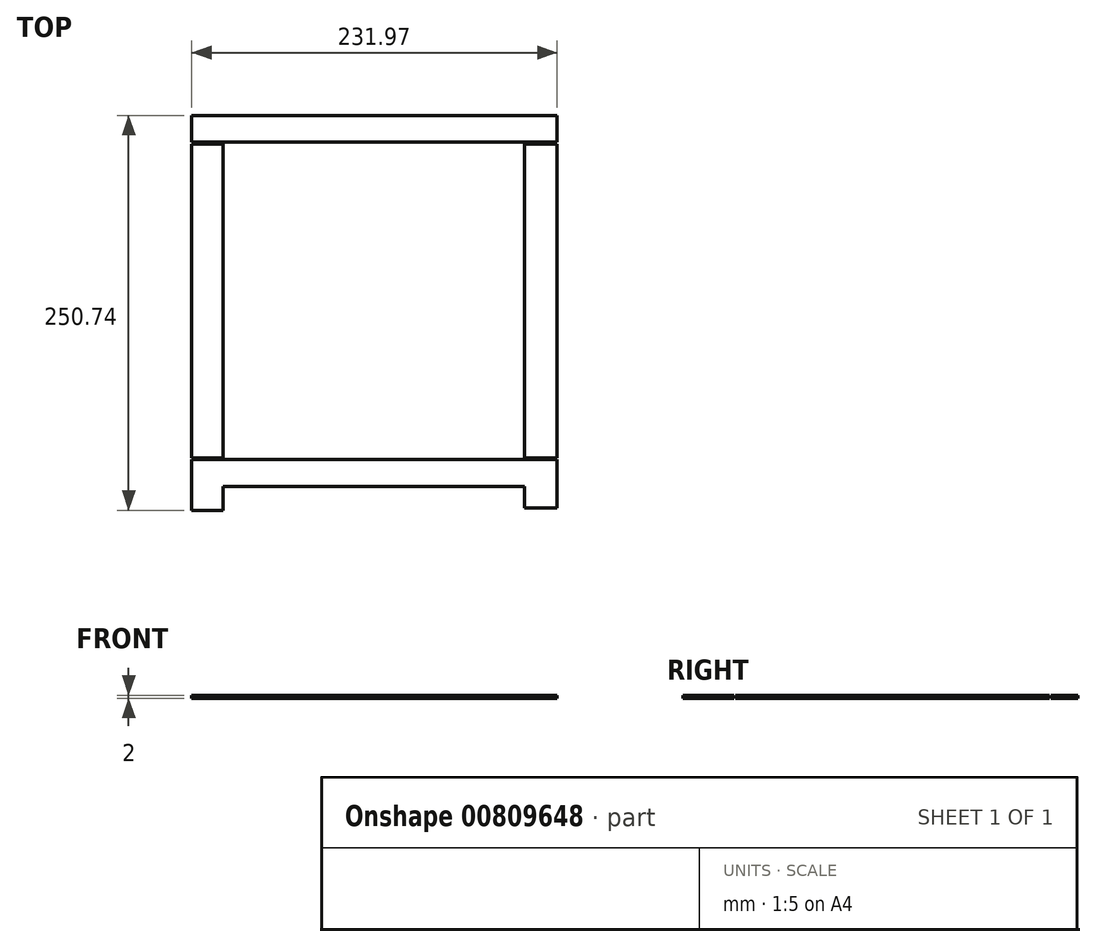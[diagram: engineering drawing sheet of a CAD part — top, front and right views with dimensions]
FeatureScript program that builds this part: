
annotation { "Feature Type Name" : "Feature", "Feature Type Description" : "" }
export const myFeature = defineFeature(function(context is Context, id is Id, definition is map)
    precondition{}
    {
        {
            var Q0;
            Q0=qCreatedBy(makeId("Top.planeOp"),FACE);
            var sketch = newSketch(context, id + "F0", { "sketchPlane" : qUnion([Q0])});
            skText(sketch, "E0", { "text": "團", "fontName": "NotoSansCJKtc-Regular.otf"});
            const initialGuessF0  = {"E0": [0, 0, 1, 0, 0.208]};
            skSetInitialGuess(sketch, initialGuessF0);
            skSolve(sketch);
        }
        {
            var Q0;
            Q0=makeQuery(id+"F0.imprint","IMPRINT",FACE,{"disambiguationData":[TD([[makeQuery(id+"F0.imprint","IMPRINT",EDGE,{"derivedFrom":sQuery(id+"F0.wireOp",EDGE,"E0.sketch_text.stroke-65")}),1.0]])]});
            extrude(context, id + "F1", {"entities" : qUnion([Q0]), "depth" : 2 * mm, "offsetDistance" : 25.4 * mm});
        }
        {
            var Q0;
            Q0=makeQuery(id+"F1.opExtrude","CAP_FACE",FACE,{"disambiguationData":[OSD([sQuery(id+"F0.wireOp",EDGE,"E0.sketch_text.stroke-65"),sQuery(id+"F0.wireOp",EDGE,"E0.sketch_text.stroke-66"),sQuery(id+"F0.wireOp",EDGE,"E0.sketch_text.stroke-67"),sQuery(id+"F0.wireOp",EDGE,"E0.sketch_text.stroke-68"),sQuery(id+"F0.wireOp",EDGE,"E0.sketch_text.stroke-69"),sQuery(id+"F0.wireOp",EDGE,"E0.sketch_text.stroke-70"),sQuery(id+"F0.wireOp",EDGE,"E0.sketch_text.stroke-71"),sQuery(id+"F0.wireOp",EDGE,"E0.sketch_text.stroke-72"),sQuery(id+"F0.wireOp",EDGE,"E0.sketch_text.stroke-73"),sQuery(id+"F0.wireOp",EDGE,"E0.sketch_text.stroke-74"),sQuery(id+"F0.wireOp",EDGE,"E0.sketch_text.stroke-75"),sQuery(id+"F0.wireOp",EDGE,"E0.sketch_text.stroke-76")])],"isStart":false});
            var sketch = newSketch(context, id + "F2", { "sketchPlane" : qUnion([Q0])});
            skLineSegment(sketch, "E1.bottom", {"start": v(28.62, 211.48) * mm, "end": v(260.59, 211.48) * mm});
            skLineSegment(sketch, "E1.top", {"start": v(28.62, 210.48) * mm, "end": v(260.59, 210.48) * mm});
            skLineSegment(sketch, "E1.left", {"start": v(28.62, 211.48) * mm, "end": v(28.62, 210.48) * mm});
            skLineSegment(sketch, "E1.right", {"start": v(260.59, 211.48) * mm, "end": v(260.59, 210.48) * mm});
            skLineSegment(sketch, "E2.bottom", {"start": v(260.59, 10.11) * mm, "end": v(28.62, 10.11) * mm});
            skLineSegment(sketch, "E2.top", {"start": v(260.59, 11.11) * mm, "end": v(28.62, 11.11) * mm});
            skLineSegment(sketch, "E2.left", {"start": v(260.59, 10.11) * mm, "end": v(260.59, 11.11) * mm});
            skLineSegment(sketch, "E2.right", {"start": v(28.62, 10.11) * mm, "end": v(28.62, 11.11) * mm});
            skSolve(sketch);
        }
        {
            var Q0;
            Q0 = qSketchRegion(id + "F2", true);
            extrude(context, id + "F3", {"entities" : qUnion([Q0]), "operationType" : NewBodyOperationType.REMOVE, "oppositeDirection" : true, "depth" : 25.4 * mm, "offsetDistance" : 25.4 * mm});
        }
    });
